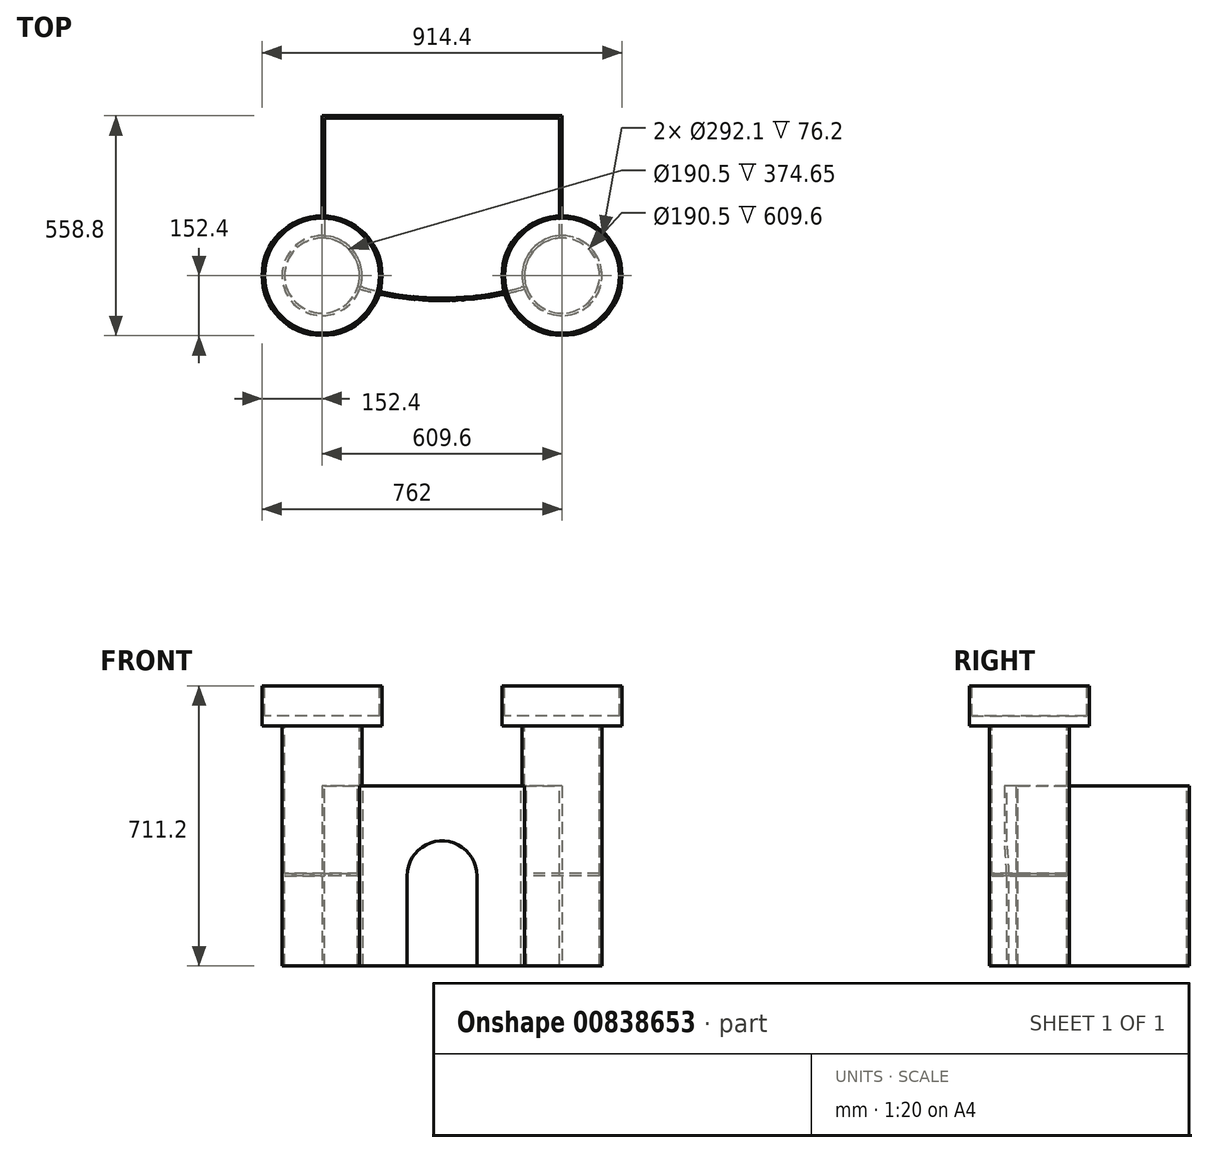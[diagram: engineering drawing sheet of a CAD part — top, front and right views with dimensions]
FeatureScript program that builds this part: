
annotation { "Feature Type Name" : "Feature", "Feature Type Description" : "" }
export const myFeature = defineFeature(function(context is Context, id is Id, definition is map)
    precondition{}
    {
        {
            var Q0;
            Q0=qCreatedBy(makeId("Top.planeOp"),FACE);
            var sketch = newSketch(context, id + "F0", { "sketchPlane" : qUnion([Q0])});
            skLineSegment(sketch, "E0.top", {"start": v(304.8, 203.2) * mm, "end": v(-304.8, 203.2) * mm});
            skLineSegment(sketch, "E0.left", {"start": v(304.8, -101.6) * mm, "end": v(304.8, 203.2) * mm});
            skLineSegment(sketch, "E0.right", {"start": v(-304.8, -101.6) * mm, "end": v(-304.8, 203.2) * mm});
            skPoint(sketch, "E0.middle", {"position": v(0, 0) * mm});
            skArc(sketch, "E1", {"start": v(-209.16, -237.48) * mm, "mid": v(0, -266.7) * mm, "end": v(209.16, -237.48) * mm});
            skArc(sketch, "E2", {"start": v(-209.16, -237.48) * mm, "mid": v(-221.72, -144.72) * mm, "end": v(-304.8, -101.6) * mm});
            skArc(sketch, "E3", {"start": v(304.8, -101.6) * mm, "mid": v(221.72, -144.72) * mm, "end": v(209.16, -237.48) * mm});
            skSolve(sketch);
        }
        {
            var Q0;
            Q0 = qSketchRegion(id + "F0", true);
            extrude(context, id + "F1", {"entities" : qUnion([Q0]), "endBound" : BoundingType.SYMMETRIC, "depth" : 457.2 * mm, "offsetDistance" : 25.4 * mm});
        }
        {
            var Q0;
            Q0=makeQuery(id+"F1.opExtrude","CAP_FACE",FACE,{"disambiguationData":[OSD([sQuery(id+"F0.wireOp",EDGE,"E0.top"),sQuery(id+"F0.wireOp",EDGE,"E0.left"),sQuery(id+"F0.wireOp",EDGE,"E0.right"),sQuery(id+"F0.wireOp",EDGE,"E1"),sQuery(id+"F0.wireOp",EDGE,"E2"),sQuery(id+"F0.wireOp",EDGE,"E3")])],"isStart":false});
            var sketch = newSketch(context, id + "F2", { "sketchPlane" : qUnion([Q0])});
            skCircle(sketch, "E4", {"center": v(304.8, -203.2) * mm, "radius": 101.6 * mm});
            skPoint(sketch, "E4.first.point", {"position": v(304.8, -101.6) * mm});
            skPoint(sketch, "E4.second.point", {"position": v(209.16, -237.48) * mm});
            skPoint(sketch, "E4.third.point", {"position": v(387.1, -262.77) * mm});
            skCircle(sketch, "E5", {"center": v(-304.8, -203.2) * mm, "radius": 101.6 * mm});
            skPoint(sketch, "E5.first.point", {"position": v(-304.8, -101.6) * mm});
            skPoint(sketch, "E5.second.point", {"position": v(-209.16, -237.48) * mm});
            skPoint(sketch, "E5.third.point", {"position": v(-364.05, -285.74) * mm});
            skSolve(sketch);
        }
        {
            var Q0;
            Q0 = qSketchRegion(id + "F2", true);
            extrude(context, id + "F3", {"entities" : qUnion([Q0]), "operationType" : NewBodyOperationType.ADD, "endBound" : BoundingType.SYMMETRIC, "depth" : 914.4 * mm, "offsetDistance" : 25.4 * mm});
        }
        {
            var Q0;
            Q0=makeQuery(id+"F3.opExtrude","CAP_FACE",FACE,{"disambiguationData":[OSD([sQuery(id+"F2.wireOp",EDGE,"E4")])],"isStart":false});
            var sketch = newSketch(context, id + "F4", { "sketchPlane" : qUnion([Q0])});
            skSolve(sketch);
        }
        {
            var Q0;
            Q0 = qSketchRegion(id + "F4", true);
            var Q1;
            Q1=makeQuery(id+"F4.imprint","IMPRINT",FACE,{"disambiguationData":[TD([[makeQuery(id+"F4.imprint","IMPRINT",EDGE,{"derivedFrom":makeQuery(id+"F3.opExtrude","CAP_EDGE",EDGE,{"disambiguationData":[OSD([sQuery(id+"F2.wireOp",EDGE,"E4")])],"isStart":false})}),1.0]])]});
            extrude(context, id + "F5", {"entities" : qUnion([Q0, Q1]), "operationType" : NewBodyOperationType.REMOVE, "oppositeDirection" : true, "depth" : 304.8 * mm, "offsetDistance" : 25.4 * mm});
        }
        {
            var Q0;
            Q0=makeQuery(id+"F3.opExtrude","CAP_FACE",FACE,{"disambiguationData":[OSD([sQuery(id+"F2.wireOp",EDGE,"E5")])],"isStart":false});
            var sketch = newSketch(context, id + "F6", { "sketchPlane" : qUnion([Q0])});
            skSolve(sketch);
        }
        {
            var Q0;
            Q0 = qSketchRegion(id + "F6", true);
            var Q1;
            Q1=makeQuery(id+"F6.imprint","IMPRINT",FACE,{"disambiguationData":[TD([[makeQuery(id+"F6.imprint","IMPRINT",EDGE,{"derivedFrom":makeQuery(id+"F3.opExtrude","CAP_EDGE",EDGE,{"disambiguationData":[OSD([sQuery(id+"F2.wireOp",EDGE,"E5")])],"isStart":false})}),1.0]])]});
            extrude(context, id + "F7", {"entities" : qUnion([Q0, Q1]), "operationType" : NewBodyOperationType.REMOVE, "oppositeDirection" : true, "depth" : 304.8 * mm, "offsetDistance" : 25.4 * mm});
        }
        {
            var Q0;
            Q0=makeQuery(id+"F7.boolean.opBoolean","COPY",FACE,{"derivedFrom":makeQuery(id+"F7.opExtrude","CAP_FACE",FACE,{"disambiguationData":[OSD([sQuery(id+"F2.wireOp",EDGE,"E5")])],"isStart":false})});
            var sketch = newSketch(context, id + "F8", { "sketchPlane" : qUnion([Q0])});
            skLineSegment(sketch, "E6.0", {"start": v(-298.45, 196.85) * mm, "end": v(-298.45, -95.44) * mm});
            skArc(sketch, "E6.1", {"start": v(-201.09, -233.15) * mm, "mid": v(0, -260.35) * mm, "end": v(201.09, -233.15) * mm});
            skArc(sketch, "E6.2", {"start": v(201.09, -233.15) * mm, "mid": v(216.65, -140.88) * mm, "end": v(298.45, -95.44) * mm});
            skArc(sketch, "E6.3", {"start": v(-298.45, -95.44) * mm, "mid": v(-216.65, -140.88) * mm, "end": v(-201.09, -233.15) * mm});
            skLineSegment(sketch, "E6.4", {"start": v(298.45, -95.44) * mm, "end": v(298.45, 196.85) * mm});
            skLineSegment(sketch, "E6.5", {"start": v(298.45, 196.85) * mm, "end": v(-298.45, 196.85) * mm});
            skSolve(sketch);
        }
        {
            var Q0;
            Q0 = qSketchRegion(id + "F8", true);
            extrude(context, id + "F9", {"entities" : qUnion([Q0]), "operationType" : NewBodyOperationType.REMOVE, "endBound" : BoundingType.THROUGH_ALL, "oppositeDirection" : true, "depth" : 25.4 * mm, "offsetDistance" : 25.4 * mm});
        }
        {
            var Q0;
            Q0=makeQuery(id+"F5.boolean.opBoolean","COPY",FACE,{"derivedFrom":makeQuery(id+"F5.opExtrude","CAP_FACE",FACE,{"disambiguationData":[OSD([sQuery(id+"F2.wireOp",EDGE,"E4")])],"isStart":false})});
            var sketch = newSketch(context, id + "F10", { "sketchPlane" : qUnion([Q0])});
            skCircle(sketch, "E7.0", {"center": v(304.8, -203.2) * mm, "radius": 95.25 * mm});
            skCircle(sketch, "E8.0", {"center": v(-304.8, -203.2) * mm, "radius": 95.25 * mm});
            skSolve(sketch);
        }
        {
            var Q0;
            Q0 = qSketchRegion(id + "F10", true);
            extrude(context, id + "F11", {"entities" : qUnion([Q0]), "operationType" : NewBodyOperationType.REMOVE, "endBound" : BoundingType.THROUGH_ALL, "oppositeDirection" : true, "depth" : 25.4 * mm, "offsetDistance" : 25.4 * mm});
        }
        {
            var Q0;
            Q0=makeQuery(id+"F5.boolean.opBoolean","COPY",FACE,{"derivedFrom":makeQuery(id+"F5.opExtrude","CAP_FACE",FACE,{"disambiguationData":[OSD([sQuery(id+"F2.wireOp",EDGE,"E4")])],"isStart":false})});
            var sketch = newSketch(context, id + "F12", { "sketchPlane" : qUnion([Q0])});
            skCircle(sketch, "E9.0", {"center": v(304.8, -203.2) * mm, "radius": 152.4 * mm});
            skCircle(sketch, "E10.0", {"center": v(-304.8, -203.2) * mm, "radius": 152.4 * mm});
            skSolve(sketch);
        }
        {
            var Q0;
            Q0 = qSketchRegion(id + "F12", true);
            extrude(context, id + "F13", {"entities" : qUnion([Q0]), "operationType" : NewBodyOperationType.ADD, "depth" : 101.6 * mm, "offsetDistance" : 25.4 * mm});
        }
        {
            var Q0;
            Q0=makeQuery(id+"F13.opExtrude","CAP_FACE",FACE,{"disambiguationData":[OSD([sQuery(id+"F12.wireOp",EDGE,"E10.0")])],"isStart":false});
            var sketch = newSketch(context, id + "F14", { "sketchPlane" : qUnion([Q0])});
            skCircle(sketch, "E11.0", {"center": v(-304.8, -203.2) * mm, "radius": 146.05 * mm});
            skCircle(sketch, "E12.0", {"center": v(304.8, -203.2) * mm, "radius": 146.05 * mm});
            skSolve(sketch);
        }
        {
            var Q0;
            Q0 = qSketchRegion(id + "F14", true);
            extrude(context, id + "F15", {"entities" : qUnion([Q0]), "operationType" : NewBodyOperationType.REMOVE, "oppositeDirection" : true, "depth" : 76.2 * mm, "offsetDistance" : 25.4 * mm});
        }
        {
            var Q0;
            Q0=qCreatedBy(makeId("Front.planeOp"),FACE);
            var sketch = newSketch(context, id + "F16", { "sketchPlane" : qUnion([Q0])});
            skArc(sketch, "E13", {"start": v(89.01, 0) * mm, "mid": v(0, 89.01) * mm, "end": v(-89.01, 0) * mm});
            skLineSegment(sketch, "E14.top", {"start": v(-89.01, -228.6) * mm, "end": v(89.01, -228.6) * mm});
            skLineSegment(sketch, "E14.left", {"start": v(-89.01, 0) * mm, "end": v(-89.01, -228.6) * mm});
            skLineSegment(sketch, "E14.right", {"start": v(89.01, 0) * mm, "end": v(89.01, -228.6) * mm});
            skSolve(sketch);
        }
        {
            var Q0;
            Q0 = qSketchRegion(id + "F16", true);
            extrude(context, id + "F17", {"entities" : qUnion([Q0]), "operationType" : NewBodyOperationType.REMOVE, "depth" : 447.04 * mm, "offsetDistance" : 25.4 * mm});
        }
        {
            var Q0;
            Q0=makeQuery(id+"F9.boolean.opBoolean","COPY",FACE,{"derivedFrom":makeQuery(id+"F9.opExtrude","SWEPT_FACE",FACE,{"disambiguationData":[OSD([sQuery(id+"F8.wireOp",EDGE,"E6.5")])]})});
            extrude(context, id + "F18", {"entities" : qUnion([Q0]), "operationType" : NewBodyOperationType.REMOVE, "depth" : 429.26 * mm, "offsetDistance" : 25.4 * mm});
        }
        {
            var Q0;
            Q0=qCreatedBy(makeId("Top.planeOp"),FACE);
            var sketch = newSketch(context, id + "F19", { "sketchPlane" : qUnion([Q0])});
            skCircle(sketch, "E15.0", {"center": v(-304.8, -203.2) * mm, "radius": 95.25 * mm});
            skCircle(sketch, "E16.0", {"center": v(304.8, -203.2) * mm, "radius": 95.25 * mm});
            skSolve(sketch);
        }
        {
            var Q0;
            Q0 = qSketchRegion(id + "F19", true);
            extrude(context, id + "F20", {"entities" : qUnion([Q0]), "operationType" : NewBodyOperationType.ADD, "depth" : 6.35 * mm, "offsetDistance" : 25.4 * mm});
        }
    });
